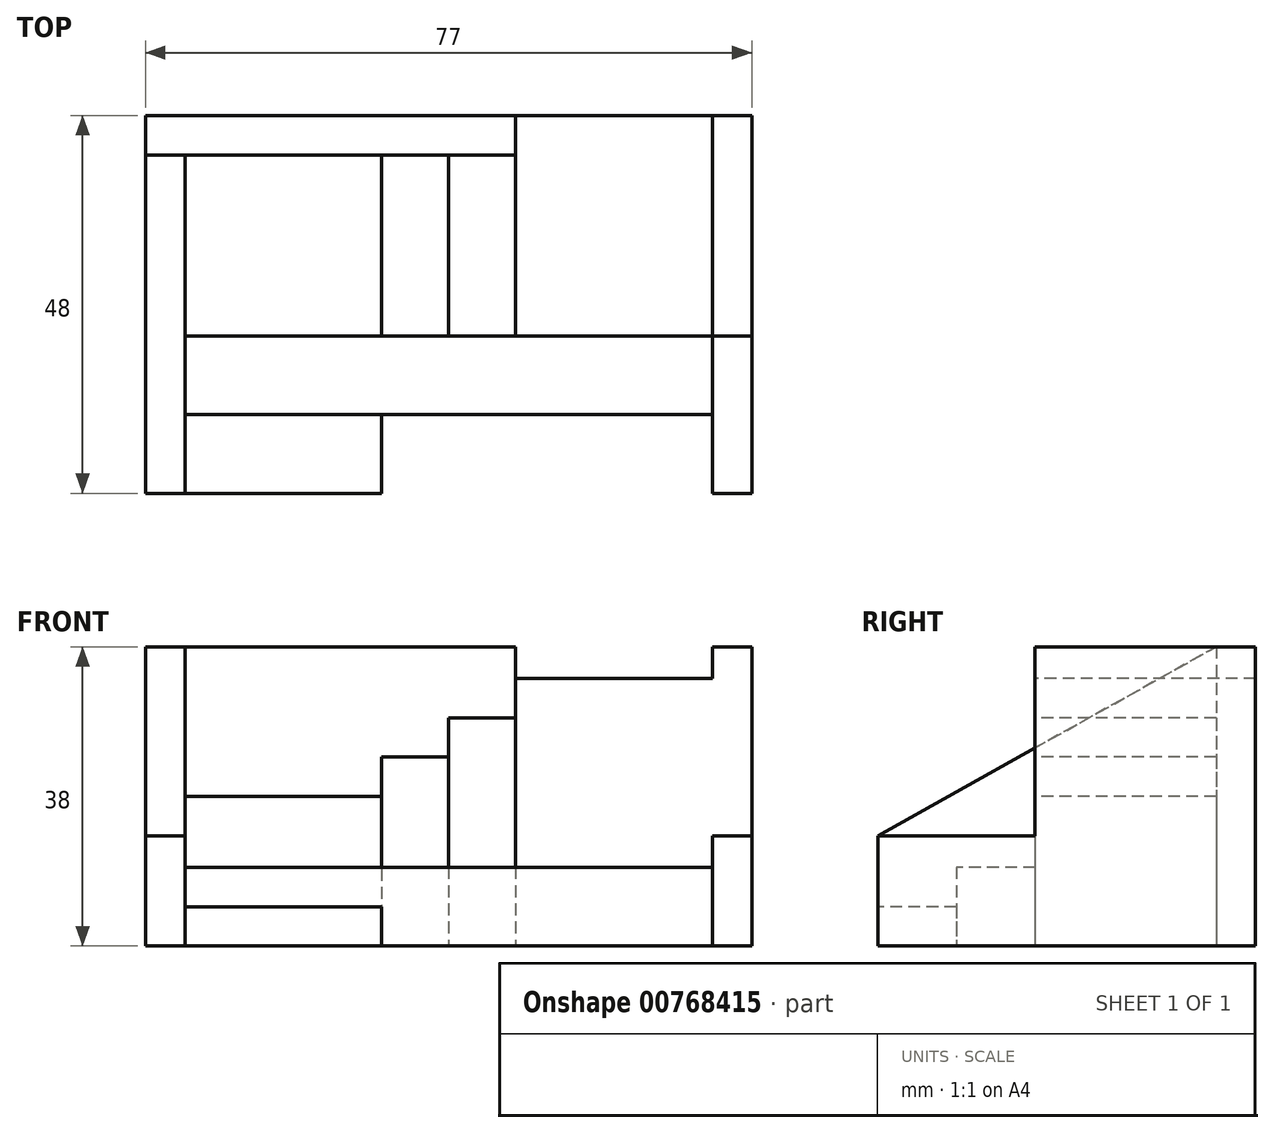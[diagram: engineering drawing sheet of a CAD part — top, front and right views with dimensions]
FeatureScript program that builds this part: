
annotation { "Feature Type Name" : "Feature", "Feature Type Description" : "" }
export const myFeature = defineFeature(function(context is Context, id is Id, definition is map)
    precondition{}
    {
        {
            var Q0;
            Q0=qCreatedBy(makeId("Top.planeOp"),FACE);
            var sketch = newSketch(context, id + "F0", { "sketchPlane" : qUnion([Q0])});
            skLineSegment(sketch, "E0.bottom", {"start": v(38.5, -24) * mm, "end": v(33.5, -24) * mm});
            skLineSegment(sketch, "E0.top", {"start": v(38.5, 24) * mm, "end": v(-38.5, 24) * mm});
            skLineSegment(sketch, "E0.left", {"start": v(38.5, -24) * mm, "end": v(38.5, 24) * mm});
            skLineSegment(sketch, "E0.right", {"start": v(-38.5, -24) * mm, "end": v(-38.5, 24) * mm});
            skPoint(sketch, "E0.middle", {"position": v(0, 0) * mm});
            skLineSegment(sketch, "E1", {"start": v(-33.5, 19) * mm, "end": v(-33.5, -24) * mm});
            skLineSegment(sketch, "E2", {"start": v(-38.5, 19) * mm, "end": v(8.5, 19) * mm});
            skLineSegment(sketch, "E3", {"start": v(-33.5, -14) * mm, "end": v(33.5, -14) * mm});
            skLineSegment(sketch, "E4", {"start": v(-33.5, -4) * mm, "end": v(38.5, -4) * mm});
            skLineSegment(sketch, "E5", {"start": v(-8.5, 19) * mm, "end": v(-8.5, -4) * mm});
            skLineSegment(sketch, "E6", {"start": v(8.5, 24) * mm, "end": v(8.5, -4) * mm});
            skLineSegment(sketch, "E7", {"start": v(33.5, 24) * mm, "end": v(33.5, -24) * mm});
            skLineSegment(sketch, "E8", {"start": v(0, 19) * mm, "end": v(0, -4) * mm});
            skLineSegment(sketch, "E9.trimOffspring", {"start": v(-8.5, -24) * mm, "end": v(-38.5, -24) * mm});
            skLineSegment(sketch, "E10.trimOffspring", {"start": v(-8.5, -14) * mm, "end": v(-8.5, -24) * mm});
            skPoint(sketch, "E11.orphan", {"position": v(38.5, -14) * mm});
            skPoint(sketch, "E12.orphan", {"position": v(38.5, 19) * mm});
            skPoint(sketch, "E13.orphan", {"position": v(0, 24) * mm});
            skPoint(sketch, "E14.orphan", {"position": v(-33.5, 24) * mm});
            skPoint(sketch, "E15.orphan", {"position": v(-38.5, -14) * mm});
            skSolve(sketch);
        }
        {
            var Q0;
            {var subQ0=sQuery(id+"F0.wireOp",EDGE,"E9.trimOffspring");var subQ7=sQuery(id+"F0.wireOp",EDGE,"E0.right");var subQ8=makeQuery(id+"F0.imprint","INTERSECT",VERTEX,{"derivedFrom":[subQ7,subQ0]});Q0=makeQuery(id+"F0.imprint","IMPRINT",FACE,{"disambiguationData":[TD([[makeQuery(id+"F0.imprint","IMPRINT",EDGE,{"disambiguationData":[TD([[subQ8,-1.0]])],"derivedFrom":subQ7}),-1.0]])]});}
            extrude(context, id + "F1", {"entities" : qUnion([Q0]), "depth" : 38 * mm, "offsetDistance" : 25 * mm});
        }
        {
            var Q0;
            Q0=makeQuery(id+"F1.opExtrude","SWEPT_FACE",FACE,{"disambiguationData":[OSD([sQuery(id+"F0.wireOp",EDGE,"E1")])]});
            var sketch = newSketch(context, id + "F2", { "sketchPlane" : qUnion([Q0])});
            skLineSegment(sketch, "E16", {"start": v(-24, 14) * mm, "end": v(19, 38) * mm});
            skSolve(sketch);
        }
        {
            var Q0;
            {var subQ0=sQuery(id+"F2.wireOp",EDGE,"E16");Q0=makeQuery(id+"F2.imprint","IMPRINT",FACE,{"disambiguationData":[TD([[makeQuery(id+"F2.imprint","IMPRINT",EDGE,{"derivedFrom":subQ0}),1.0]])]});}
            extrude(context, id + "F3", {"entities" : qUnion([Q0]), "operationType" : NewBodyOperationType.REMOVE, "oppositeDirection" : true, "depth" : 25 * mm, "offsetDistance" : 25 * mm});
        }
        {
            var Q0;
            {var subQ2=sQuery(id+"F0.wireOp",EDGE,"E0.right");var subQ7=sQuery(id+"F0.wireOp",EDGE,"E0.top");var subQ9=makeQuery(id+"F0.imprint","INTERSECT",VERTEX,{"derivedFrom":[subQ7,subQ2]});Q0=makeQuery(id+"F0.imprint","IMPRINT",FACE,{"disambiguationData":[TD([[makeQuery(id+"F0.imprint","IMPRINT",EDGE,{"disambiguationData":[TD([[subQ9,1.0]])],"derivedFrom":subQ7}),1.0]])]});}
            extrude(context, id + "F4", {"entities" : qUnion([Q0]), "operationType" : NewBodyOperationType.ADD, "depth" : 38 * mm, "offsetDistance" : 25 * mm});
        }
        {
            var Q0;
            {var subQ0=sQuery(id+"F0.wireOp",EDGE,"E0.left");var subQ1=sQuery(id+"F0.wireOp",EDGE,"E0.top");var subQ2=makeQuery(id+"F0.imprint","INTERSECT",VERTEX,{"derivedFrom":[subQ1,subQ0]});Q0=makeQuery(id+"F0.imprint","IMPRINT",FACE,{"disambiguationData":[TD([[makeQuery(id+"F0.imprint","IMPRINT",EDGE,{"disambiguationData":[TD([[subQ2,-1.0]])],"derivedFrom":subQ1}),1.0]])]});}
            extrude(context, id + "F5", {"entities" : qUnion([Q0]), "depth" : 38 * mm, "offsetDistance" : 25 * mm});
        }
        {
            var Q0;
            {var subQ0=sQuery(id+"F0.wireOp",EDGE,"E6");var subQ4=sQuery(id+"F0.wireOp",EDGE,"E0.top");var subQ5=makeQuery(id+"F0.imprint","INTERSECT",VERTEX,{"derivedFrom":[subQ4,subQ0]});Q0=makeQuery(id+"F0.imprint","IMPRINT",FACE,{"disambiguationData":[TD([[makeQuery(id+"F0.imprint","IMPRINT",EDGE,{"disambiguationData":[TD([[subQ5,1.0]])],"derivedFrom":subQ4}),1.0]])]});}
            extrude(context, id + "F6", {"entities" : qUnion([Q0]), "depth" : 34 * mm, "offsetDistance" : 25 * mm});
        }
        {
            var Q0;
            {var subQ5=sQuery(id+"F0.wireOp",EDGE,"E0.bottom");Q0=makeQuery(id+"F0.imprint","IMPRINT",FACE,{"disambiguationData":[TD([[makeQuery(id+"F0.imprint","IMPRINT",EDGE,{"derivedFrom":subQ5}),-1.0]])]});}
            extrude(context, id + "F7", {"entities" : qUnion([Q0]), "operationType" : NewBodyOperationType.ADD, "depth" : 14 * mm, "offsetDistance" : 25 * mm});
        }
        {
            var Q0;
            {var subQ3=sQuery(id+"F0.wireOp",EDGE,"E8");Q0=makeQuery(id+"F0.imprint","IMPRINT",FACE,{"disambiguationData":[TD([[makeQuery(id+"F0.imprint","IMPRINT",EDGE,{"derivedFrom":subQ3}),1.0]])]});}
            extrude(context, id + "F8", {"entities" : qUnion([Q0]), "depth" : 29 * mm, "offsetDistance" : 25 * mm});
        }
        {
            var Q0;
            {var subQ0=sQuery(id+"F0.wireOp",EDGE,"E5");Q0=makeQuery(id+"F0.imprint","IMPRINT",FACE,{"disambiguationData":[TD([[makeQuery(id+"F0.imprint","IMPRINT",EDGE,{"derivedFrom":subQ0}),1.0]])]});}
            extrude(context, id + "F9", {"entities" : qUnion([Q0]), "depth" : 24 * mm, "offsetDistance" : 25 * mm});
        }
        {
            var Q0;
            {var subQ5=sQuery(id+"F0.wireOp",EDGE,"E5");Q0=makeQuery(id+"F0.imprint","IMPRINT",FACE,{"disambiguationData":[TD([[makeQuery(id+"F0.imprint","IMPRINT",EDGE,{"derivedFrom":subQ5}),-1.0]])]});}
            extrude(context, id + "F10", {"entities" : qUnion([Q0]), "depth" : 19 * mm, "offsetDistance" : 25 * mm});
        }
        {
            var Q0;
            {var subQ1=sQuery(id+"F0.wireOp",EDGE,"E1");var subQ5=sQuery(id+"F0.wireOp",EDGE,"E3");var subQ8=makeQuery(id+"F0.imprint","INTERSECT",VERTEX,{"derivedFrom":[subQ1,subQ5]});Q0=makeQuery(id+"F0.imprint","IMPRINT",FACE,{"disambiguationData":[TD([[makeQuery(id+"F0.imprint","IMPRINT",EDGE,{"disambiguationData":[TD([[subQ8,1.0]])],"derivedFrom":subQ1}),1.0]])]});}
            extrude(context, id + "F11", {"entities" : qUnion([Q0]), "depth" : 10 * mm, "offsetDistance" : 25 * mm});
        }
        {
            var Q0;
            {var subQ5=sQuery(id+"F0.wireOp",EDGE,"E10.trimOffspring");Q0=makeQuery(id+"F0.imprint","IMPRINT",FACE,{"disambiguationData":[TD([[makeQuery(id+"F0.imprint","IMPRINT",EDGE,{"derivedFrom":subQ5}),-1.0]])]});}
            extrude(context, id + "F12", {"entities" : qUnion([Q0]), "depth" : 5 * mm, "offsetDistance" : 25 * mm});
        }
    });
